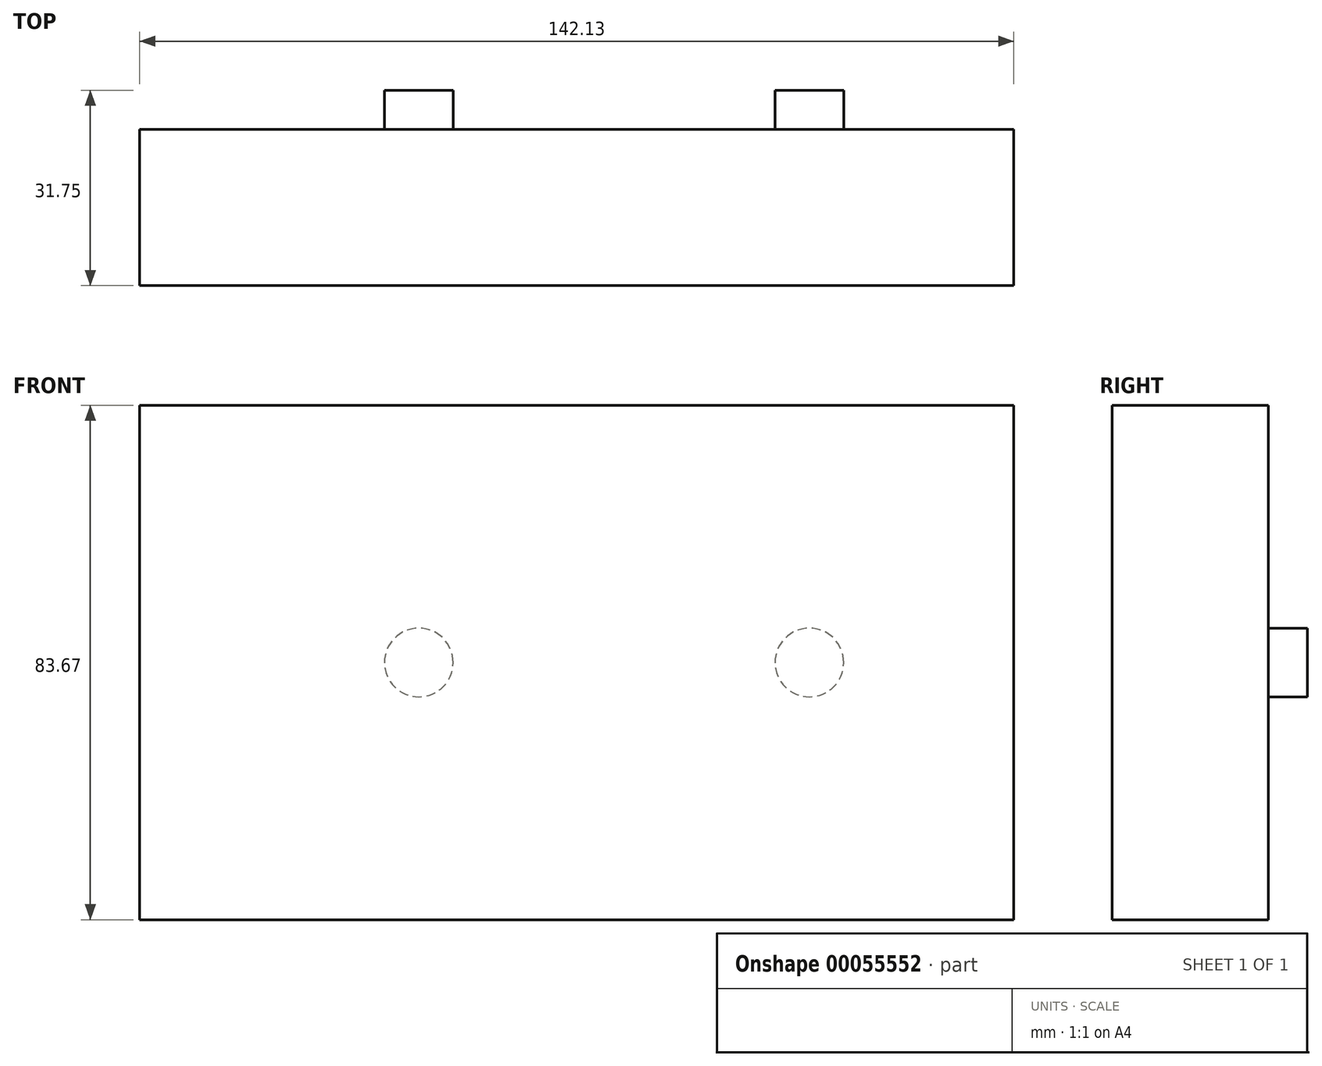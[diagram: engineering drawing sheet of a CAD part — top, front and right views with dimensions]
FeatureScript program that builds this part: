
annotation { "Feature Type Name" : "Feature", "Feature Type Description" : "" }
export const myFeature = defineFeature(function(context is Context, id is Id, definition is map)
    precondition{}
    {
        {
            var Q0;
            Q0=qCreatedBy(makeId("Front.planeOp"),FACE);
            var sketch = newSketch(context, id + "F0", { "sketchPlane" : qUnion([Q0])});
            skLineSegment(sketch, "E0.bottom", {"start": v(-53.14, -26.16) * mm, "end": v(63.59, -26.16) * mm});
            skLineSegment(sketch, "E0.top", {"start": v(-53.14, 57.5) * mm, "end": v(63.59, 57.5) * mm});
            skLineSegment(sketch, "E0.left", {"start": v(-53.14, -26.16) * mm, "end": v(-53.14, 57.5) * mm});
            skLineSegment(sketch, "E0.right", {"start": v(63.59, -26.16) * mm, "end": v(63.59, 57.5) * mm});
            skLineSegment(sketch, "E1", {"start": v(-33.16, 57.5) * mm, "end": v(-33.16, -26.16) * mm, "construction": true});
            skLineSegment(sketch, "E2", {"start": v(30.34, 57.5) * mm, "end": v(30.34, -26.16) * mm, "construction": true});
            skCircle(sketch, "E3", {"center": v(-33.16, 15.67) * mm, "radius": 5.59 * mm});
            skCircle(sketch, "E4", {"center": v(30.34, 15.67) * mm, "radius": 5.59 * mm});
            skSolve(sketch);
        }
        {
            var Q0;
            Q0 = qSketchRegion(id + "F0", true);
            var Q1;
            Q1=makeQuery(id+"F0.imprint","IMPRINT",FACE,{"disambiguationData":[TD([[makeQuery(id+"F0.imprint","IMPRINT",EDGE,{"derivedFrom":sQuery(id+"F0.wireOp",EDGE,"E3")}),1.0]])]});
            var Q2;
            Q2=makeQuery(id+"F0.imprint","IMPRINT",FACE,{"disambiguationData":[TD([[makeQuery(id+"F0.imprint","IMPRINT",EDGE,{"derivedFrom":sQuery(id+"F0.wireOp",EDGE,"E4")}),1.0]])]});
            extrude(context, id + "F1", {"entities" : qUnion([Q0, Q1, Q2]), "depth" : 25.4 * mm});
        }
        {
            var Q0;
            Q0=makeQuery(id+"F0.imprint","IMPRINT",FACE,{"disambiguationData":[TD([[makeQuery(id+"F0.imprint","IMPRINT",EDGE,{"derivedFrom":sQuery(id+"F0.wireOp",EDGE,"E4")}),1.0]])]});
            var Q1;
            Q1=makeQuery(id+"F0.imprint","IMPRINT",FACE,{"disambiguationData":[TD([[makeQuery(id+"F0.imprint","IMPRINT",EDGE,{"derivedFrom":sQuery(id+"F0.wireOp",EDGE,"E3")}),1.0]])]});
            extrude(context, id + "F2", {"entities" : qUnion([Q0, Q1]), "operationType" : NewBodyOperationType.ADD, "oppositeDirection" : true, "depth" : 6.35 * mm});
        }
        {
            var Q0;
            Q0=makeQuery(id+"F1.opExtrude","SWEPT_FACE",FACE,{"disambiguationData":[OSD([sQuery(id+"F0.wireOp",EDGE,"E0.left")])]});
            extrude(context, id + "F3", {"entities" : qUnion([Q0]), "operationType" : NewBodyOperationType.ADD, "depth" : 25.4 * mm});
        }
    });
